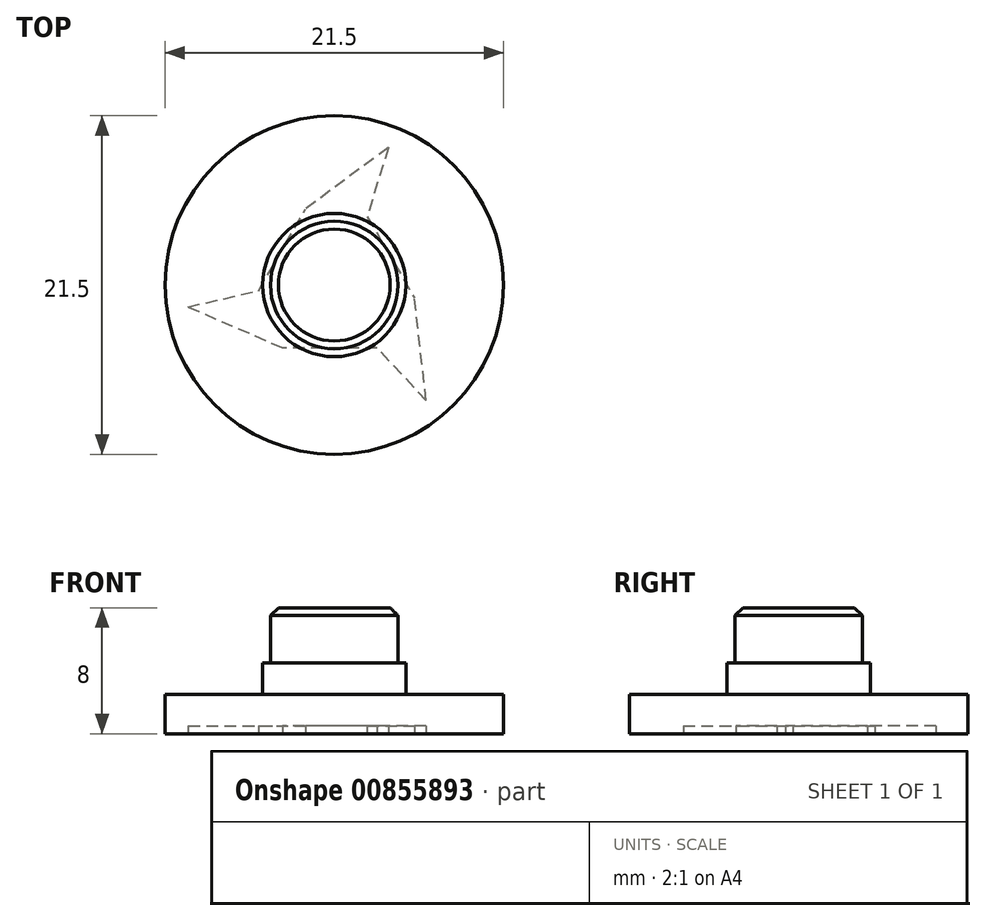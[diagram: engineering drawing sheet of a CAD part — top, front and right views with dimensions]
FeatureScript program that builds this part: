
annotation { "Feature Type Name" : "Feature", "Feature Type Description" : "" }
export const myFeature = defineFeature(function(context is Context, id is Id, definition is map)
    precondition{}
    {
        {
            var Q0;
            Q0=qCreatedBy(makeId("Top.planeOp"),FACE);
            var sketch = newSketch(context, id + "F0", { "sketchPlane" : qUnion([Q0])});
            skCircle(sketch, "E0", {"center": v(0, 0) * mm, "radius": 10 * mm});
            skLineSegment(sketch, "E1", {"start": v(0, 25) * mm, "end": v(0, -25) * mm, "construction": true});
            skLineSegment(sketch, "E2", {"start": v(-25, 0) * mm, "end": v(25, 0) * mm, "construction": true});
            skLineSegment(sketch, "E3", {"start": v(-17.68, 17.68) * mm, "end": v(0, 0) * mm, "construction": true});
            skLineSegment(sketch, "E4", {"start": v(0, 0) * mm, "end": v(17.68, -17.68) * mm, "construction": true});
            skLineSegment(sketch, "E5", {"start": v(0, 0) * mm, "end": v(17.68, 17.68) * mm, "construction": true});
            skLineSegment(sketch, "E6", {"start": v(0, 0) * mm, "end": v(-17.68, -17.68) * mm, "construction": true});
            skLineSegment(sketch, "E7", {"start": v(0, 0) * mm, "end": v(-7.65, 18.48) * mm, "construction": true});
            skLineSegment(sketch, "E8", {"start": v(0, 0) * mm, "end": v(-18.48, -7.65) * mm, "construction": true});
            skLineSegment(sketch, "E9", {"start": v(0, 0) * mm, "end": v(-7.65, -18.48) * mm, "construction": true});
            skLineSegment(sketch, "E10", {"start": v(0, 0) * mm, "end": v(7.65, -18.48) * mm, "construction": true});
            skLineSegment(sketch, "E11", {"start": v(0, 0) * mm, "end": v(18.48, -7.65) * mm, "construction": true});
            skLineSegment(sketch, "E12", {"start": v(0, 0) * mm, "end": v(18.48, 7.65) * mm, "construction": true});
            skLineSegment(sketch, "E13", {"start": v(0, 0) * mm, "end": v(7.65, 18.48) * mm, "construction": true});
            skLineSegment(sketch, "E14", {"start": v(0, 0) * mm, "end": v(-18.48, 7.65) * mm, "construction": true});
            skCircle(sketch, "E15", {"center": v(0, 0) * mm, "radius": 10.75 * mm});
            skLineSegment(sketch, "E16", {"start": v(3.43, 8.73) * mm, "end": v(2.1, 4.36) * mm});
            skLineSegment(sketch, "E17", {"start": v(5.84, -7.34) * mm, "end": v(2.73, -4) * mm});
            skLineSegment(sketch, "E18", {"start": v(-9.27, -1.4) * mm, "end": v(-4.82, -0.37) * mm});
            skLineSegment(sketch, "E19", {"start": v(-9.27, -1.4) * mm, "end": v(-4.42, -3.5) * mm});
            skLineSegment(sketch, "E20", {"start": v(5.84, -7.34) * mm, "end": v(5.24, -2.08) * mm});
            skLineSegment(sketch, "E21", {"start": v(3.43, 8.73) * mm, "end": v(-0.81, 5.58) * mm});
            skLineSegment(sketch, "E22", {"start": v(2.73, -4) * mm, "end": v(-3.27, -4) * mm});
            skLineSegment(sketch, "E23", {"start": v(-4.42, -3.5) * mm, "end": v(-3.27, -4) * mm});
            skLineSegment(sketch, "E24", {"start": v(-4.82, -0.37) * mm, "end": v(-1.82, 4.83) * mm});
            skLineSegment(sketch, "E25", {"start": v(-0.81, 5.58) * mm, "end": v(-1.82, 4.83) * mm});
            skLineSegment(sketch, "E26", {"start": v(2.1, 4.36) * mm, "end": v(5.1, -0.84) * mm});
            skLineSegment(sketch, "E27", {"start": v(5.24, -2.08) * mm, "end": v(5.1, -0.84) * mm});
            skSolve(sketch);
        }
        {
            var Q0;
            Q0=qSketchRegion(id+"F0",true);
            var Q1;
            Q1=makeQuery(id+"F0.imprint","IMPRINT",FACE,{"disambiguationData":[TD([[makeQuery(id+"F0.imprint","IMPRINT",EDGE,{"derivedFrom":sQuery(id+"F0.wireOp",EDGE,"E0")}),1.0]])]});
            var Q2;
            Q2=makeQuery(id+"F0.imprint","IMPRINT",FACE,{"disambiguationData":[TD([[makeQuery(id+"F0.imprint","IMPRINT",EDGE,{"derivedFrom":sQuery(id+"F0.wireOp",EDGE,"jN2jA10u-DtFZ-AHMn-O0dh-Xupn0wcTT4Cn")}),-1.0]])]});
            var Q3;
            Q3=makeQuery(id+"F0.imprint","IMPRINT",FACE,{"disambiguationData":[TD([[makeQuery(id+"F0.imprint","IMPRINT",EDGE,{"derivedFrom":sQuery(id+"F0.wireOp",EDGE,"E16")}),-1.0]])]});
            extrude(context, id + "F1", {"entities" : qUnion([Q0, Q1, Q2, Q3]), "depth" : 2.5 * mm, "offsetDistance" : 25 * mm});
        }
        {
            var Q0;
            Q0=makeQuery(id+"F1.opExtrude","CAP_FACE",FACE,{"disambiguationData":[OSD([sQuery(id+"F0.wireOp",EDGE,"E15")])],"isStart":false});
            var sketch = newSketch(context, id + "F2", { "sketchPlane" : qUnion([Q0])});
            skCircle(sketch, "E28", {"center": v(0, 0) * mm, "radius": 4.05 * mm});
            skSolve(sketch);
        }
        {
            var Q0;
            Q0=qSketchRegion(id+"F2",true);
            extrude(context, id + "F3", {"entities" : qUnion([Q0]), "operationType" : NewBodyOperationType.ADD, "depth" : 5.5 * mm, "offsetDistance" : 25 * mm});
        }
        {
            var Q0;
            Q0=makeQuery(id+"F3.opExtrude","CAP_EDGE",EDGE,{"disambiguationData":[OSD([sQuery(id+"F2.wireOp",EDGE,"E28")])],"isStart":false});
            var Q1;
            Q1=makeQuery(id+"F1.opExtrude","CAP_EDGE",EDGE,{"disambiguationData":[OSD([sQuery(id+"F0.wireOp",EDGE,"281bee0e-2aea-47b7-b4e1-999b86a55542.4.0")])],"isStart":true});
            var Q2;
            Q2=makeQuery(id+"F1.opExtrude","CAP_EDGE",EDGE,{"disambiguationData":[OSD([sQuery(id+"F0.wireOp",EDGE,"281bee0e-2aea-47b7-b4e1-999b86a55542.3.1")])],"isStart":true});
            var Q3;
            Q3=makeQuery(id+"F1.opExtrude","CAP_EDGE",EDGE,{"disambiguationData":[OSD([sQuery(id+"F0.wireOp",EDGE,"281bee0e-2aea-47b7-b4e1-999b86a55542.3.0")])],"isStart":true});
            var Q4;
            Q4=makeQuery(id+"F1.opExtrude","CAP_EDGE",EDGE,{"disambiguationData":[OSD([sQuery(id+"F0.wireOp",EDGE,"281bee0e-2aea-47b7-b4e1-999b86a55542.2.1")])],"isStart":true});
            var Q5;
            Q5=makeQuery(id+"F1.opExtrude","CAP_EDGE",EDGE,{"disambiguationData":[OSD([sQuery(id+"F0.wireOp",EDGE,"281bee0e-2aea-47b7-b4e1-999b86a55542.2.0")])],"isStart":true});
            var Q6;
            Q6=makeQuery(id+"F1.opExtrude","CAP_EDGE",EDGE,{"disambiguationData":[OSD([sQuery(id+"F0.wireOp",EDGE,"281bee0e-2aea-47b7-b4e1-999b86a55542.1.1")])],"isStart":true});
            var Q7;
            Q7=makeQuery(id+"F1.opExtrude","CAP_EDGE",EDGE,{"disambiguationData":[OSD([sQuery(id+"F0.wireOp",EDGE,"281bee0e-2aea-47b7-b4e1-999b86a55542.1.0")])],"isStart":true});
            var Q8;
            Q8=makeQuery(id+"F1.opExtrude","CAP_EDGE",EDGE,{"disambiguationData":[OSD([sQuery(id+"F0.wireOp",EDGE,"VJwDG1Qv-JdYY-zPm5-o4WR-dzW4zfFZ494p")])],"isStart":true});
            var Q9;
            Q9=makeQuery(id+"F1.opExtrude","CAP_EDGE",EDGE,{"disambiguationData":[OSD([sQuery(id+"F0.wireOp",EDGE,"Lo3pglTx-e1UP-W00b-ypUq-am2WEzU7Gj5O")])],"isStart":true});
            var Q10;
            Q10=makeQuery(id+"F1.opExtrude","CAP_EDGE",EDGE,{"disambiguationData":[OSD([sQuery(id+"F0.wireOp",EDGE,"281bee0e-2aea-47b7-b4e1-999b86a55542.5.1")])],"isStart":true});
            var Q11;
            Q11=makeQuery(id+"F1.opExtrude","CAP_EDGE",EDGE,{"disambiguationData":[OSD([sQuery(id+"F0.wireOp",EDGE,"281bee0e-2aea-47b7-b4e1-999b86a55542.5.0")])],"isStart":true});
            var Q12;
            Q12=makeQuery(id+"F1.opExtrude","CAP_EDGE",EDGE,{"disambiguationData":[OSD([sQuery(id+"F0.wireOp",EDGE,"281bee0e-2aea-47b7-b4e1-999b86a55542.4.1")])],"isStart":true});
            chamfer(context, id + "F4", {"entities" : qUnion([Q0, Q1, Q2, Q3, Q4, Q5, Q6, Q7, Q8, Q9, Q10, Q11, Q12]), "width" : 0.5 * mm, "tangentPropagation" : true});
        }
        {
            var Q0;
            Q0=makeQuery(id+"F1.opExtrude","CAP_FACE",FACE,{"disambiguationData":[OSD([sQuery(id+"F0.wireOp",EDGE,"E15")])],"isStart":false});
            var sketch = newSketch(context, id + "F5", { "sketchPlane" : qUnion([Q0])});
            skCircle(sketch, "E29", {"center": v(0, 0) * mm, "radius": 4.55 * mm});
            skSolve(sketch);
        }
        {
            var Q0;
            Q0=qSketchRegion(id+"F5",true);
            extrude(context, id + "F6", {"entities" : qUnion([Q0]), "operationType" : NewBodyOperationType.ADD, "depth" : 2 * mm, "offsetDistance" : 25 * mm});
        }
        {
            var Q0;
            Q0=makeQuery(id+"F0.imprint","IMPRINT",FACE,{"disambiguationData":[TD([[makeQuery(id+"F0.imprint","IMPRINT",EDGE,{"derivedFrom":sQuery(id+"F0.wireOp",EDGE,"E16")}),-1.0]])]});
            extrude(context, id + "F7", {"entities" : qUnion([Q0]), "operationType" : NewBodyOperationType.REMOVE, "depth" : 0.5 * mm, "offsetDistance" : 25 * mm});
        }
    });
